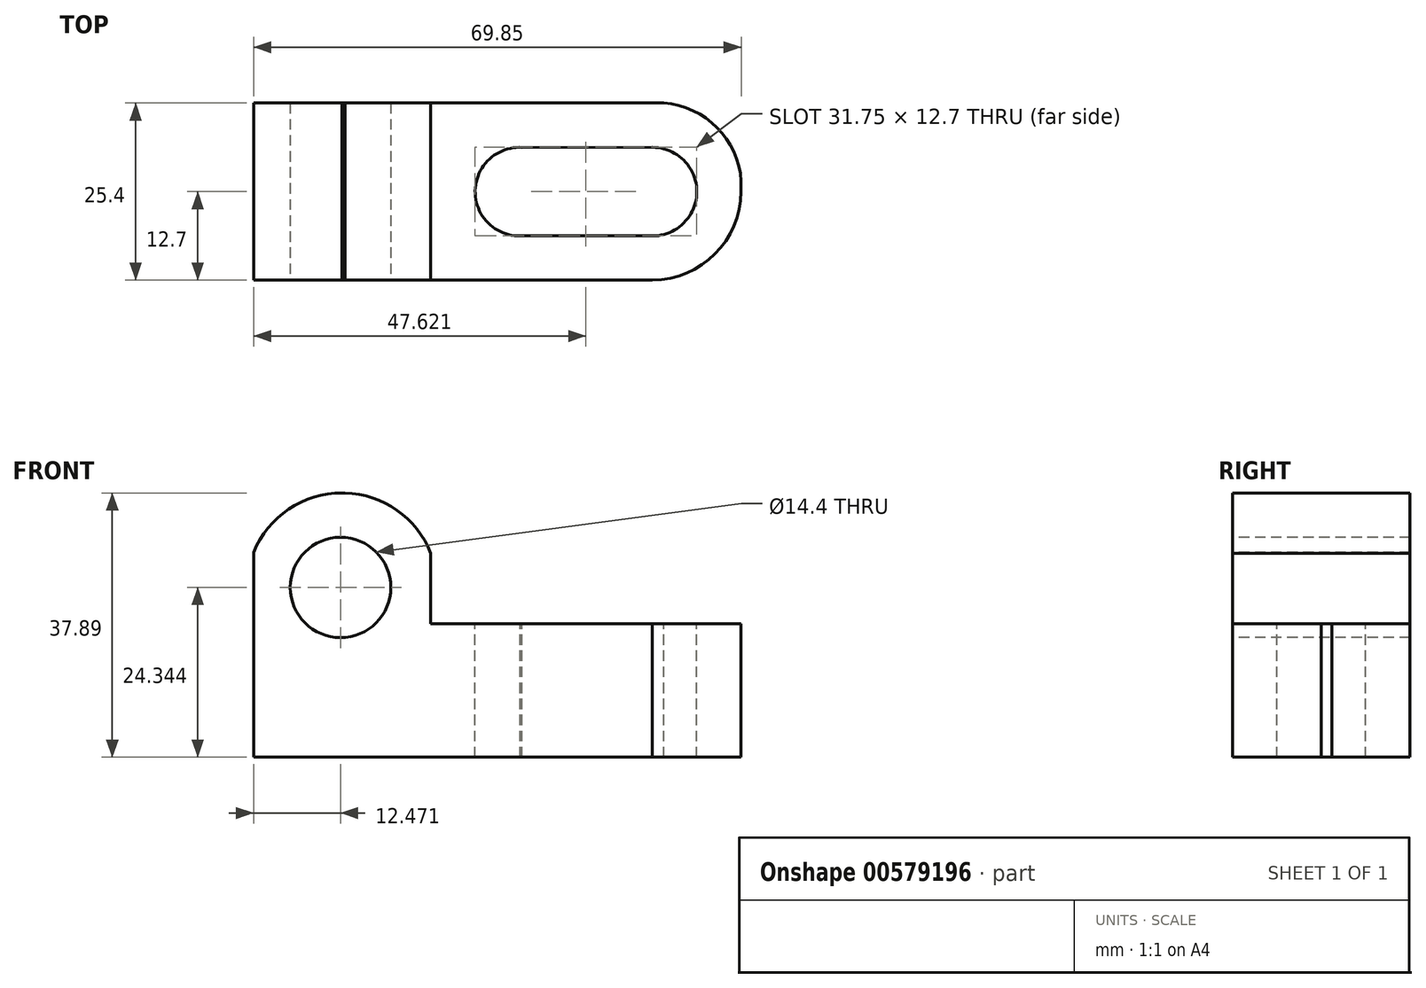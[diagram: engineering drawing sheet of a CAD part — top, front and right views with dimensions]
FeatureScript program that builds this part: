
annotation { "Feature Type Name" : "Feature", "Feature Type Description" : "" }
export const myFeature = defineFeature(function(context is Context, id is Id, definition is map)
    precondition{}
    {
        {
            var Q0;
            Q0=qCreatedBy(makeId("Front.planeOp"),FACE);
            var sketch = newSketch(context, id + "F0", { "sketchPlane" : qUnion([Q0])});
            skLineSegment(sketch, "E0", {"start": v(-70.57, 50.13) * mm, "end": v(-70.57, 12.03) * mm});
            skLineSegment(sketch, "E1", {"start": v(-70.57, 12.03) * mm, "end": v(-0.72, 12.03) * mm});
            skLineSegment(sketch, "E2", {"start": v(-0.72, 11.27) * mm, "end": v(-0.72, 31.17) * mm});
            skLineSegment(sketch, "E3", {"start": v(-0.72, 31.17) * mm, "end": v(-45.17, 31.17) * mm});
            skLineSegment(sketch, "E4", {"start": v(-45.17, 31.17) * mm, "end": v(-45.17, 49.71) * mm});
            skLineSegment(sketch, "E5", {"start": v(-45.17, 49.71) * mm, "end": v(-70.57, 50.13) * mm});
            skSolve(sketch);
        }
        {
            var Q0;
            {var subQ4=sQuery(id+"F0.wireOp",EDGE,"E0");Q0=makeQuery(id+"F0.imprint","IMPRINT",FACE,{"disambiguationData":[TD([[makeQuery(id+"F0.imprint","IMPRINT",EDGE,{"derivedFrom":subQ4}),1.0]])]});}
            extrude(context, id + "F1", {"entities" : qUnion([Q0]), "depth" : 25.4 * mm, "offsetDistance" : 25.4 * mm});
        }
        {
            var Q0;
            Q0=makeQuery(id+"F1.opExtrude","SWEPT_FACE",FACE,{"disambiguationData":[OSD([sQuery(id+"F0.wireOp",EDGE,"E3")])]});
            var sketch = newSketch(context, id + "F2", { "sketchPlane" : qUnion([Q0])});
            skCircle(sketch, "E6", {"center": v(-13.42, -12.7) * mm, "radius": 6.35 * mm});
            skCircle(sketch, "E7", {"center": v(-32.47, -12.7) * mm, "radius": 6.35 * mm});
            skSolve(sketch);
        }
        {
            var Q0;
            Q0=makeQuery(id+"F2.imprint","IMPRINT",FACE,{"disambiguationData":[TD([[makeQuery(id+"F2.imprint","IMPRINT",EDGE,{"derivedFrom":sQuery(id+"F2.wireOp",EDGE,"E7")}),1.0]])]});
            var Q1;
            Q1=makeQuery(id+"F2.imprint","IMPRINT",FACE,{"disambiguationData":[TD([[makeQuery(id+"F2.imprint","IMPRINT",EDGE,{"derivedFrom":sQuery(id+"F2.wireOp",EDGE,"E6")}),1.0]])]});
            extrude(context, id + "F3", {"entities" : qUnion([Q0, Q1]), "operationType" : NewBodyOperationType.REMOVE, "endBound" : BoundingType.THROUGH_ALL, "oppositeDirection" : true, "depth" : 25.4 * mm, "offsetDistance" : 25.4 * mm});
        }
        {
            var Q0;
            Q0=makeQuery(id+"F1.opExtrude","SWEPT_FACE",FACE,{"disambiguationData":[OSD([sQuery(id+"F0.wireOp",EDGE,"E3")])]});
            var sketch = newSketch(context, id + "F4", { "sketchPlane" : qUnion([Q0])});
            skLineSegment(sketch, "E8", {"start": v(-32.87, -6.36) * mm, "end": v(-13.43, -6.35) * mm});
            skLineSegment(sketch, "E9", {"start": v(-32.6, -19.05) * mm, "end": v(-13.42, -19.05) * mm});
            skSolve(sketch);
        }
        {
            var Q0;
            {var subQ0=sQuery(id+"F4.wireOp",EDGE,"E8");var subQ1=makeQuery(id+"F3.boolean.opBoolean","COPY",EDGE,{"derivedFrom":makeQuery(id+"F3.opExtrude","CAP_EDGE",EDGE,{"disambiguationData":[OSD([sQuery(id+"F2.wireOp",EDGE,"E6")])],"isStart":true})});var subQ2=makeQuery(id+"F4.imprint","INTERSECT",VERTEX,{"derivedFrom":[subQ1,subQ0]});Q0=makeQuery(id+"F4.imprint","IMPRINT",FACE,{"disambiguationData":[TD([[makeQuery(id+"F4.imprint","IMPRINT",EDGE,{"disambiguationData":[TD([[subQ2,1.0]])],"derivedFrom":subQ0}),-1.0]])]});}
            extrude(context, id + "F5", {"entities" : qUnion([Q0]), "operationType" : NewBodyOperationType.REMOVE, "endBound" : BoundingType.THROUGH_ALL, "oppositeDirection" : true, "depth" : 25.4 * mm, "offsetDistance" : 25.4 * mm});
        }
        {
            var Q0;
            Q0=makeQuery(id+"F1.opExtrude","CAP_FACE",FACE,{"disambiguationData":[OSD([sQuery(id+"F0.wireOp",EDGE,"E0"),sQuery(id+"F0.wireOp",EDGE,"E1"),sQuery(id+"F0.wireOp",EDGE,"E2"),sQuery(id+"F0.wireOp",EDGE,"E3"),sQuery(id+"F0.wireOp",EDGE,"E4"),sQuery(id+"F0.wireOp",EDGE,"E5")])],"isStart":false});
            var sketch = newSketch(context, id + "F6", { "sketchPlane" : qUnion([Q0])});
            skCircle(sketch, "E10", {"center": v(-58.1, 36.37) * mm, "radius": 7.2 * mm});
            skSolve(sketch);
        }
        {
            var Q0;
            Q0=makeQuery(id+"F6.imprint","IMPRINT",FACE,{"disambiguationData":[TD([[makeQuery(id+"F6.imprint","IMPRINT",EDGE,{"derivedFrom":sQuery(id+"F6.wireOp",EDGE,"E10")}),1.0]])]});
            extrude(context, id + "F7", {"entities" : qUnion([Q0]), "operationType" : NewBodyOperationType.REMOVE, "endBound" : BoundingType.THROUGH_ALL, "oppositeDirection" : true, "depth" : 25.4 * mm, "offsetDistance" : 25.4 * mm});
        }
        {
            var Q0;
            Q0=makeQuery(id+"F1.opExtrude","CAP_FACE",FACE,{"disambiguationData":[OSD([sQuery(id+"F0.wireOp",EDGE,"E0"),sQuery(id+"F0.wireOp",EDGE,"E1"),sQuery(id+"F0.wireOp",EDGE,"E2"),sQuery(id+"F0.wireOp",EDGE,"E3"),sQuery(id+"F0.wireOp",EDGE,"E4"),sQuery(id+"F0.wireOp",EDGE,"E5")])],"isStart":false});
            var sketch = newSketch(context, id + "F8", { "sketchPlane" : qUnion([Q0])});
            skArc(sketch, "E11", {"start": v(-45.17, 31.17) * mm, "mid": v(-57.94, 49.92) * mm, "end": v(-70.57, 31.08) * mm});
            skSolve(sketch);
        }
        {
            var Q0;
            {var subQ0=sQuery(id+"F8.wireOp",EDGE,"E11");var subQ1=makeQuery(id+"F1.opExtrude","CAP_EDGE",EDGE,{"disambiguationData":[OSD([sQuery(id+"F0.wireOp",EDGE,"E4")])],"isStart":false});var subQ2=makeQuery(id+"F8.imprint","INTERSECT",VERTEX,{"derivedFrom":[subQ1,subQ0]});Q0=makeQuery(id+"F8.imprint","IMPRINT",FACE,{"disambiguationData":[TD([[makeQuery(id+"F8.imprint","IMPRINT",EDGE,{"disambiguationData":[TD([[subQ2,-1.0]])],"derivedFrom":subQ0}),-1.0]])]});}
            var Q1;
            {var subQ0=sQuery(id+"F8.wireOp",EDGE,"E11");var subQ1=makeQuery(id+"F1.opExtrude","CAP_EDGE",EDGE,{"disambiguationData":[OSD([sQuery(id+"F0.wireOp",EDGE,"E5")])],"isStart":false});var subQ2=makeQuery(id+"F8.imprint","INTERSECT",VERTEX,{"disambiguationData":[OD(1.0)],"derivedFrom":[subQ1,subQ0]});Q1=makeQuery(id+"F8.imprint","IMPRINT",FACE,{"disambiguationData":[TD([[makeQuery(id+"F8.imprint","IMPRINT",EDGE,{"disambiguationData":[TD([[subQ2,-1.0]])],"derivedFrom":subQ0}),-1.0]])]});}
            extrude(context, id + "F9", {"entities" : qUnion([Q0, Q1]), "operationType" : NewBodyOperationType.REMOVE, "oppositeDirection" : true, "depth" : 25.4 * mm, "offsetDistance" : 25.4 * mm});
        }
        {
            var Q0;
            Q0=makeQuery(id+"F1.opExtrude","SWEPT_FACE",FACE,{"disambiguationData":[OSD([sQuery(id+"F0.wireOp",EDGE,"E3")])]});
            var sketch = newSketch(context, id + "F10", { "sketchPlane" : qUnion([Q0])});
            skArc(sketch, "E12", {"start": v(-0.72, -12.7) * mm, "mid": v(-4.25, -3.44) * mm, "end": v(-13.55, 0) * mm});
            skArc(sketch, "E13", {"start": v(-13.42, -25.4) * mm, "mid": v(-4.49, -21.64) * mm, "end": v(-0.72, -12.7) * mm});
            skSolve(sketch);
        }
        {
            var Q0;
            {var subQ0=sQuery(id+"F10.wireOp",EDGE,"E12");var subQ1=sQuery(id+"F0.wireOp",EDGE,"E3");var subQ4=makeQuery(id+"F1.opExtrude","CAP_EDGE",EDGE,{"disambiguationData":[OSD([subQ1])],"isStart":true});var subQ5=makeQuery(id+"F10.imprint","INTERSECT",VERTEX,{"disambiguationData":[OD(1.0)],"derivedFrom":[subQ4,subQ0]});Q0=makeQuery(id+"F10.imprint","IMPRINT",FACE,{"disambiguationData":[TD([[makeQuery(id+"F10.imprint","IMPRINT",EDGE,{"disambiguationData":[TD([[subQ5,1.0]])],"derivedFrom":subQ0}),-1.0]])]});}
            var Q1;
            {var subQ0=sQuery(id+"F10.wireOp",EDGE,"E13");Q1=makeQuery(id+"F10.imprint","IMPRINT",FACE,{"disambiguationData":[TD([[makeQuery(id+"F10.imprint","IMPRINT",EDGE,{"derivedFrom":subQ0}),-1.0]])]});}
            extrude(context, id + "F11", {"entities" : qUnion([Q0, Q1]), "operationType" : NewBodyOperationType.REMOVE, "endBound" : BoundingType.THROUGH_ALL, "oppositeDirection" : true, "depth" : 25.4 * mm, "offsetDistance" : 25.4 * mm});
        }
    });
